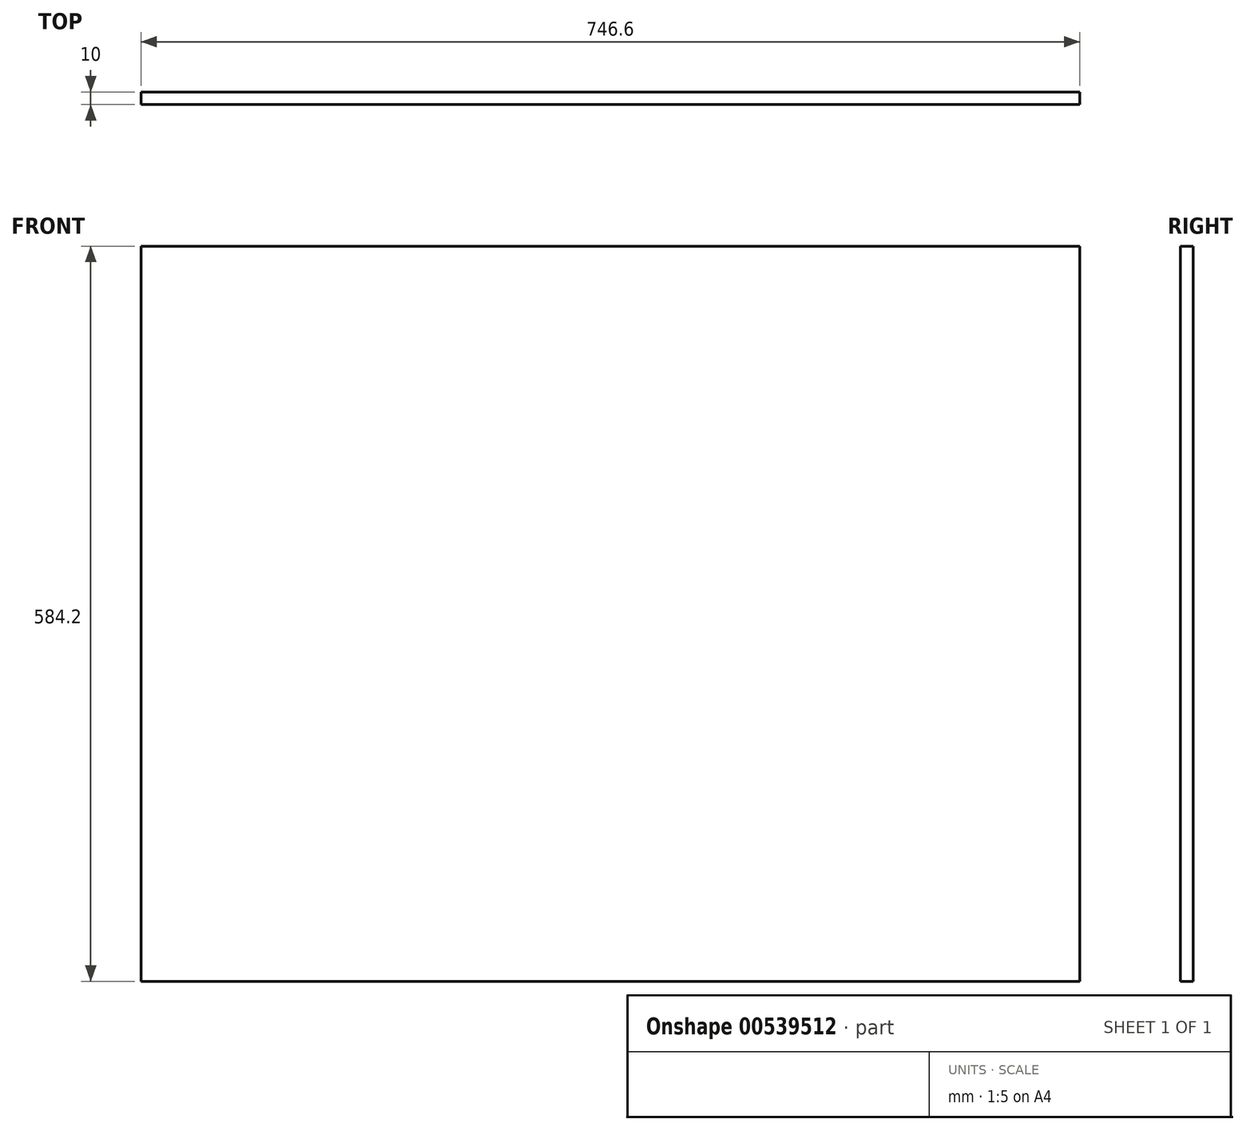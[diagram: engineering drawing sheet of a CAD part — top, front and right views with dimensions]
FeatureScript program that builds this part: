
annotation { "Feature Type Name" : "Feature", "Feature Type Description" : "" }
export const myFeature = defineFeature(function(context is Context, id is Id, definition is map)
    precondition{}
    {
        {
            var Q0;
            Q0=qCreatedBy(makeId("Front.planeOp"),FACE);
            var sketch = newSketch(context, id + "F0", { "sketchPlane" : qUnion([Q0])});
            skLineSegment(sketch, "E0.bottom", {"start": v(373.3, -292.1) * mm, "end": v(-373.3, -292.1) * mm});
            skLineSegment(sketch, "E0.top", {"start": v(373.3, 292.1) * mm, "end": v(-373.3, 292.1) * mm});
            skLineSegment(sketch, "E0.left", {"start": v(373.3, -292.1) * mm, "end": v(373.3, 292.1) * mm});
            skLineSegment(sketch, "E0.right", {"start": v(-373.3, -292.1) * mm, "end": v(-373.3, 292.1) * mm});
            skPoint(sketch, "E0.middle", {"position": v(0, 0) * mm});
            skSolve(sketch);
        }
        {
            var Q0;
            Q0=makeQuery(id+"F0.imprint","IMPRINT",FACE,{"disambiguationData":[TD([[makeQuery(id+"F0.imprint","IMPRINT",EDGE,{"derivedFrom":sQuery(id+"F0.wireOp",EDGE,"E0.bottom")}),-1.0]])]});
            extrude(context, id + "F1", {"entities" : qUnion([Q0]), "depth" : 10 * mm});
        }
    });
